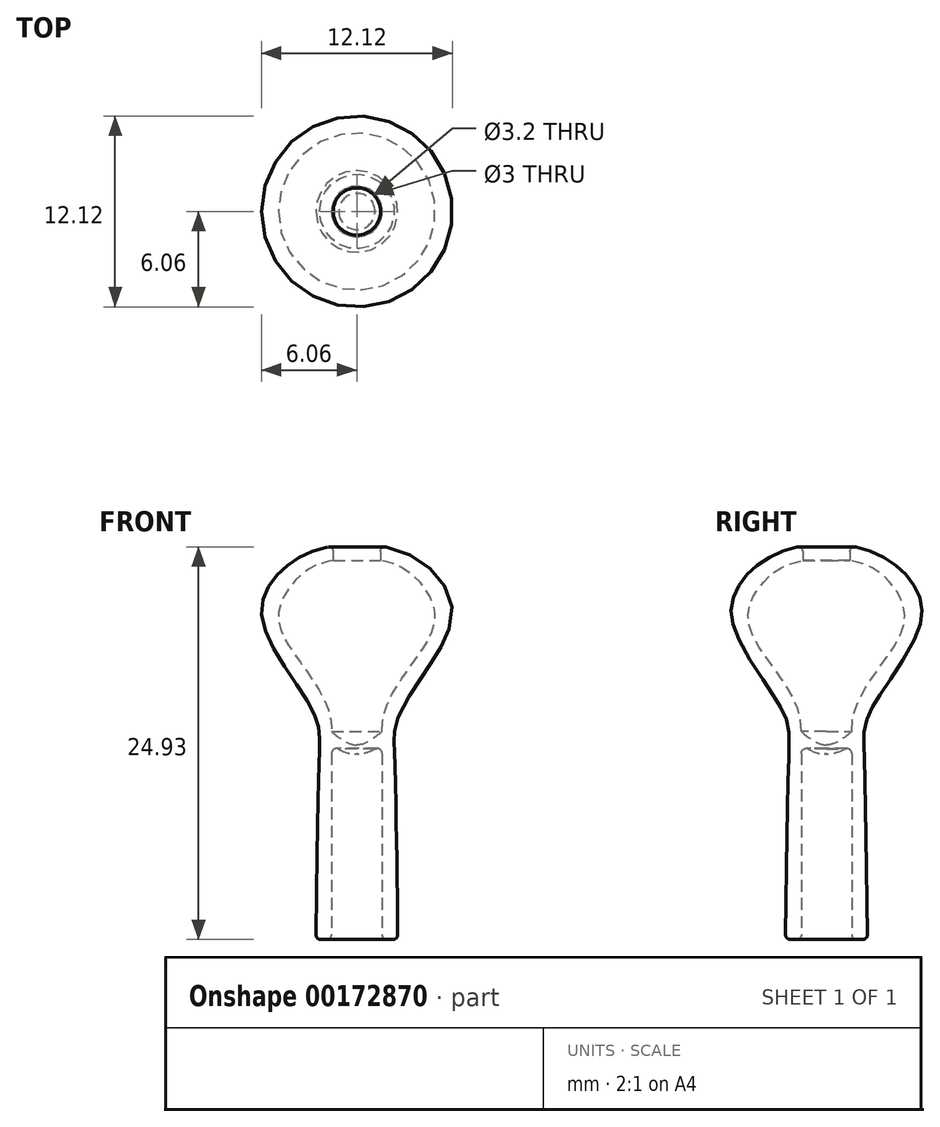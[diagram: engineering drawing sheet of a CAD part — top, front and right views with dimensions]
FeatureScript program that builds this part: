
annotation { "Feature Type Name" : "Feature", "Feature Type Description" : "" }
export const myFeature = defineFeature(function(context is Context, id is Id, definition is map)
    precondition{}
    {
        {
            var Q0;
            Q0=qCreatedBy(makeId("Front.planeOp"),FACE);
            var sketch = newSketch(context, id + "F0", { "sketchPlane" : qUnion([Q0])});
            skLineSegment(sketch, "E0", {"start": v(0, 0) * mm, "end": v(0, 25) * mm, "construction": true});
            skLineSegment(sketch, "E1.0", {"start": v(1.6, 0) * mm, "end": v(1.6, 13.23) * mm});
            skLineSegment(sketch, "E2.0", {"start": v(6, 0) * mm, "end": v(6, 25) * mm, "construction": true});
            skLineSegment(sketch, "E3", {"start": v(1.6, 0) * mm, "end": v(2.6, 0) * mm});
            skFitSpline(sketch, "E4", {"points": [v(1.5, 25) * mm, v(4.81, 23.4) * mm, v(6, 20.26) * mm, v(2.81, 14.56) * mm, v(2.38, 12.06) * mm, v(2.6, 0) * mm], "startDerivative": vector(25.47, -4.7) * mm, "endDerivative": vector(0.6, -70.61) * mm});
            skFitSpline(sketch, "E5", {"points": [v(1.6, 13.23) * mm, v(0.92, 12.68) * mm, v(0.33, 12.4) * mm, v(0, 12.35) * mm], "startDerivative": vector(-1.4, -1.5) * mm, "endDerivative": vector(-1.22, -0.06) * mm});
            skFitSpline(sketch, "E6.0", {"points": [v(1.96, 12.74) * mm, v(1.9, 12.68) * mm, v(1.77, 12.56) * mm, v(1.55, 12.36) * mm, v(1.34, 12.2) * mm, v(1.16, 12.1) * mm, v(0.97, 12) * mm, v(0.78, 11.91) * mm, v(0.6, 11.85) * mm, v(0.4, 11.8) * mm, v(0.18, 11.78) * mm, v(0.05, 11.78) * mm, v(0, 11.78) * mm]});
            skLineSegment(sketch, "E7", {"start": v(0, 12.35) * mm, "end": v(0, 11.78) * mm});
            skLineSegment(sketch, "E8", {"start": v(1.5, 24.07) * mm, "end": v(1.5, 25) * mm});
            skFitSpline(sketch, "E9", {"points": [v(1.5, 24.07) * mm, v(3.13, 23.47) * mm, v(4.97, 20.78) * mm, v(3.6, 17.6) * mm, v(1.6, 13.23) * mm], "startDerivative": vector(7.21, -1.6) * mm, "endDerivative": vector(0.47, -16) * mm});
            skSolve(sketch);
        }
        {
            var Q0;
            Q0 = qSketchRegion(id + "F0", true);
            var Q1;
            Q1=sQuery(id+"F0.wireOp",EDGE,"E0");
            revolve(context, id + "F1", {"entities" : qUnion([Q0]), "axis" : qUnion([Q1]), "revolveType" : RevolveType.FULL});
        }
        {
            var Q0;
            Q0=makeQuery(id+"F1.opRevolve","SWEPT_EDGE",EDGE,{"disambiguationData":[OSD([sQuery(id+"F0.wireOp",EDGE,"E3"),sQuery(id+"F0.wireOp",EDGE,"E4")])]});
            var Q1;
            Q1=makeQuery(id+"F1.opRevolve","SWEPT_EDGE",EDGE,{"disambiguationData":[OSD([sQuery(id+"F0.wireOp",EDGE,"E1.0"),sQuery(id+"F0.wireOp",EDGE,"E3")])]});
            var Q2;
            Q2=makeQuery(id+"F1.opRevolve","SWEPT_EDGE",EDGE,{"disambiguationData":[OSD([sQuery(id+"F0.wireOp",EDGE,"E1.0"),sQuery(id+"F0.wireOp",EDGE,"E4")])]});
            fillet(context, id + "F2", {"entities" : qUnion([Q0, Q1, Q2]), "radius" : .3 * mm, "tangentPropagation" : true, "allowEdgeOverflow" : false});
        }
    });
